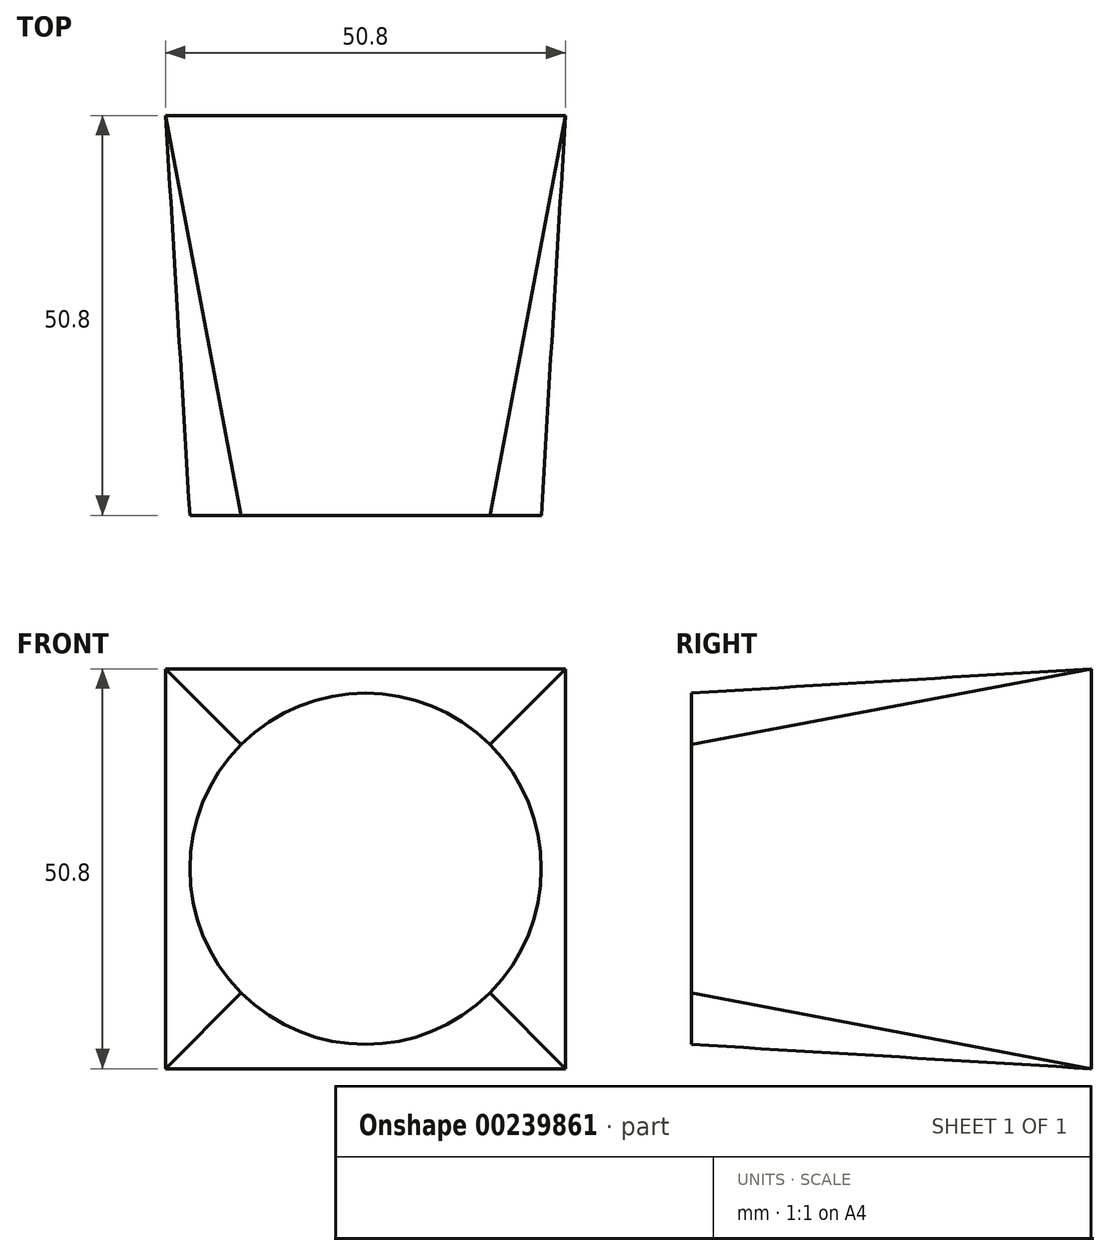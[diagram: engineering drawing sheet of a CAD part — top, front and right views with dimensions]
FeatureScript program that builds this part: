
annotation { "Feature Type Name" : "Feature", "Feature Type Description" : "" }
export const myFeature = defineFeature(function(context is Context, id is Id, definition is map)
    precondition{}
    {
        {
            var Q0;
            Q0=qCreatedBy(makeId("Front.planeOp"),FACE);
            var sketch = newSketch(context, id + "F0", { "sketchPlane" : qUnion([Q0])});
            skLineSegment(sketch, "E0.bottom", {"start": v(25.4, 25.4) * mm, "end": v(-25.4, 25.4) * mm});
            skLineSegment(sketch, "E0.top", {"start": v(25.4, -25.4) * mm, "end": v(-25.4, -25.4) * mm});
            skLineSegment(sketch, "E0.left", {"start": v(25.4, 25.4) * mm, "end": v(25.4, -25.4) * mm});
            skLineSegment(sketch, "E0.right", {"start": v(-25.4, 25.4) * mm, "end": v(-25.4, -25.4) * mm});
            skPoint(sketch, "E0.middle", {"position": v(0, 0) * mm});
            skSolve(sketch);
        }
        {
            var Q0;
            Q0=qCreatedBy(makeId("Front.planeOp"),FACE);
            cPlane(context, id + "F1", {"entities" : qUnion([Q0]), "cplaneType" : CPlaneType.OFFSET, "offset" : 50.8 * mm, "width" : 152.4 * mm, "height" : 152.4 * mm});
        }
        {
            var Q0;
            Q0=qCreatedBy(id+"F1.planeOp",FACE);
            var sketch = newSketch(context, id + "F2", { "sketchPlane" : qUnion([Q0])});
            skCircle(sketch, "E1", {"center": v(0, 0) * mm, "radius": 22.32 * mm});
            skSolve(sketch);
        }
        {
            var Q0;
            Q0=makeQuery(id+"F0.imprint","IMPRINT",FACE,{"disambiguationData":[TD([[makeQuery(id+"F0.imprint","IMPRINT",EDGE,{"derivedFrom":sQuery(id+"F0.wireOp",EDGE,"E0.bottom")}),1.0]])]});
            var Q1;
            Q1=makeQuery(id+"F2.imprint","IMPRINT",FACE,{"disambiguationData":[TD([[makeQuery(id+"F2.imprint","IMPRINT",EDGE,{"derivedFrom":sQuery(id+"F2.wireOp",EDGE,"E1")}),1.0]])]});
            loft(context, id + "F3", {"sheetProfilesArray" : [{ "sheetProfileEntities" : qUnion([Q0]) }, { "sheetProfileEntities" : qUnion([Q1]) }]});
        }
    });
